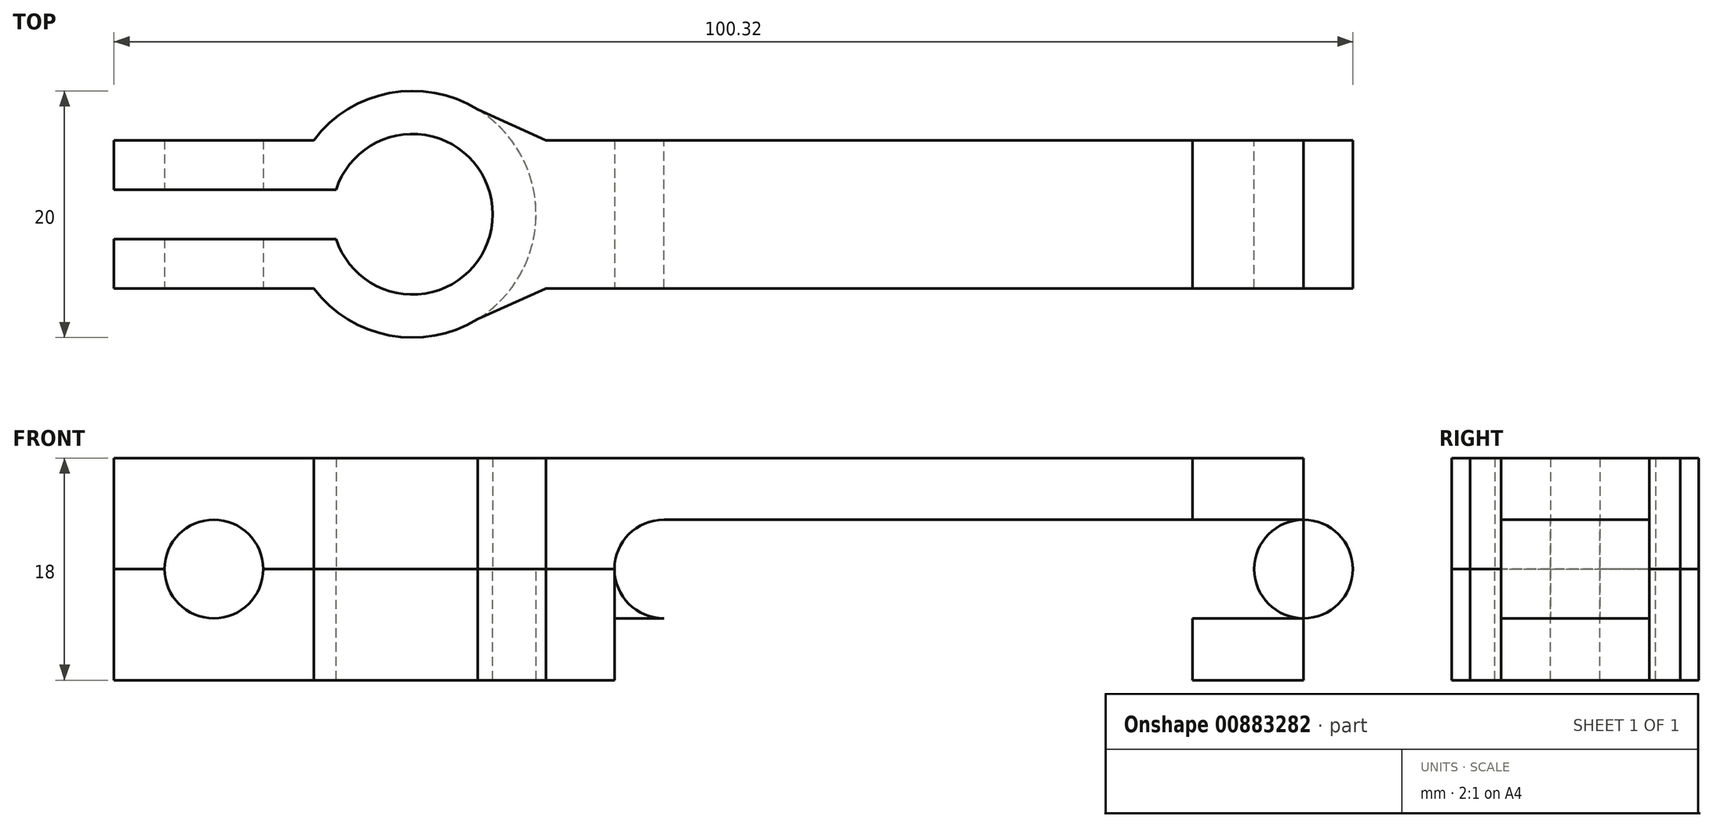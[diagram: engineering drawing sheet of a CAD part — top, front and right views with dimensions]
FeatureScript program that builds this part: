
annotation { "Feature Type Name" : "Feature", "Feature Type Description" : "" }
export const myFeature = defineFeature(function(context is Context, id is Id, definition is map)
    precondition{}
    {
        {
            var Q0;
            Q0=qCreatedBy(makeId("Top.planeOp"),FACE);
            var sketch = newSketch(context, id + "F0", { "sketchPlane" : qUnion([Q0])});
            skLineSegment(sketch, "E0", {"start": v(16.35, 0) * mm, "end": v(16.35, 6) * mm});
            skLineSegment(sketch, "E1", {"start": v(16.35, 6) * mm, "end": v(16.35, -6) * mm});
            skLineSegment(sketch, "E2", {"start": v(12.35, 0) * mm, "end": v(63.15, 0) * mm});
            skLineSegment(sketch, "E3", {"start": v(16.35, 6) * mm, "end": v(62.2, 6) * mm});
            skLineSegment(sketch, "E4", {"start": v(16.35, -6) * mm, "end": v(62.2, -6) * mm});
            skLineSegment(sketch, "E5", {"start": v(81.15, -2.5) * mm, "end": v(81.15, 2.5) * mm});
            skLineSegment(sketch, "E6", {"start": v(-8.1, 2) * mm, "end": v(-24.17, 2) * mm});
            skLineSegment(sketch, "E7", {"start": v(-8.1, -2) * mm, "end": v(-24.17, -2) * mm});
            skLineSegment(sketch, "E8", {"start": v(64.1, 2.5) * mm, "end": v(81.15, 2.5) * mm});
            skLineSegment(sketch, "E9.MirrorCS", {"start": v(64.1, -2.5) * mm, "end": v(81.15, -2.5) * mm});
            skLineSegment(sketch, "E10", {"start": v(63.15, 5.05) * mm, "end": v(63.15, 3.45) * mm});
            skLineSegment(sketch, "E11", {"start": v(63.15, -3.45) * mm, "end": v(63.15, -5.05) * mm});
            skPoint(sketch, "E12.visualSharp", {"position": v(63.15, 2.5) * mm});
            skPoint(sketch, "E13.visualSharp", {"position": v(63.15, -2.5) * mm});
            skPoint(sketch, "E14.visualSharp", {"position": v(63.15, -6) * mm});
            skPoint(sketch, "E15.visualSharp", {"position": v(63.15, 6) * mm});
            skLineSegment(sketch, "E16", {"start": v(63.15, 3.45) * mm, "end": v(63.15, -3.45) * mm});
            skLineSegment(sketch, "E17", {"start": v(63.15, 2.5) * mm, "end": v(64.1, 2.5) * mm});
            skLineSegment(sketch, "E18", {"start": v(64.1, -2.5) * mm, "end": v(63.15, -2.5) * mm});
            skLineSegment(sketch, "E19", {"start": v(62.2, -6) * mm, "end": v(63.15, -6) * mm});
            skLineSegment(sketch, "E20", {"start": v(63.15, -5.05) * mm, "end": v(63.15, -6) * mm});
            skLineSegment(sketch, "E21", {"start": v(62.2, 6) * mm, "end": v(63.15, 6) * mm});
            skLineSegment(sketch, "E22", {"start": v(63.15, 5.05) * mm, "end": v(63.15, 6) * mm});
            skArc(sketch, "E23", {"start": v(-6.18, -2) * mm, "mid": v(6.5, 0) * mm, "end": v(-6.18, 2) * mm});
            skLineSegment(sketch, "E24", {"start": v(-8.1, 2) * mm, "end": v(-6.18, 2) * mm});
            skLineSegment(sketch, "E25", {"start": v(-8.1, -2) * mm, "end": v(-6.18, -2) * mm});
            skLineSegment(sketch, "E26", {"start": v(-10.17, -7) * mm, "end": v(-24.17, -7) * mm});
            skLineSegment(sketch, "E27.trimOffspring", {"start": v(-24.17, 2) * mm, "end": v(-24.17, 6) * mm});
            skArc(sketch, "E28", {"start": v(-8, -6) * mm, "mid": v(10, 0) * mm, "end": v(-8, 6) * mm});
            skLineSegment(sketch, "E29", {"start": v(16.35, -6) * mm, "end": v(10.8, -6) * mm});
            skLineSegment(sketch, "E30", {"start": v(10.8, -6) * mm, "end": v(5.28, -8.5) * mm});
            skLineSegment(sketch, "E31.MirrorCS", {"start": v(16.35, 6) * mm, "end": v(10.8, 6) * mm});
            skLineSegment(sketch, "E32.MirrorCS", {"start": v(10.8, 6) * mm, "end": v(5.28, 8.5) * mm});
            skLineSegment(sketch, "E33", {"start": v(-24.17, 6) * mm, "end": v(-8, 6) * mm});
            skLineSegment(sketch, "E34.MirrorCS", {"start": v(-24.17, -6) * mm, "end": v(-8, -6) * mm});
            skLineSegment(sketch, "E35.MirrorCS", {"start": v(-24.17, -2) * mm, "end": v(-24.17, -6) * mm});
            skSolve(sketch);
        }
        {
            var Q0;
            Q0=makeQuery(id+"F0.imprint","IMPRINT",FACE,{"disambiguationData":[TD([[makeQuery(id+"F0.imprint","IMPRINT",EDGE,{"derivedFrom":sQuery(id+"F0.wireOp",EDGE,"E6")}),-1.0]])]});
            extrude(context, id + "F1", {"entities" : qUnion([Q0]), "depth" : 9 * mm, "offsetDistance" : 25 * mm});
        }
        {
            var Q0;
            {var subQ4=sQuery(id+"F0.wireOp",EDGE,"E1");Q0=makeQuery(id+"F0.imprint","IMPRINT",FACE,{"disambiguationData":[TD([[makeQuery(id+"F0.imprint","IMPRINT",EDGE,{"derivedFrom":subQ4}),1.0]])]});}
            var Q1;
            {var subQ4=sQuery(id+"F0.wireOp",EDGE,"E0");Q1=makeQuery(id+"F0.imprint","IMPRINT",FACE,{"disambiguationData":[TD([[makeQuery(id+"F0.imprint","IMPRINT",EDGE,{"derivedFrom":subQ4}),-1.0]])]});}
            var Q2;
            {var subQ0=sQuery(id+"F0.wireOp",EDGE,"26rSQapK-BJur-WUPp-nK8w-Sfx6okr37QMO");Q2=makeQuery(id+"F0.imprint","IMPRINT",FACE,{"disambiguationData":[TD([[makeQuery(id+"F0.imprint","IMPRINT",EDGE,{"derivedFrom":subQ0}),-1.0]])]});}
            var Q3;
            {var subQ0=sQuery(id+"F0.wireOp",EDGE,"FH9L3wZH-bFjv-XjhE-hYi4-qwH4n2wXpiqg");Q3=makeQuery(id+"F0.imprint","IMPRINT",FACE,{"disambiguationData":[TD([[makeQuery(id+"F0.imprint","IMPRINT",EDGE,{"derivedFrom":subQ0}),1.0]])]});}
            extrude(context, id + "F2", {"entities" : qUnion([Q0, Q1, Q2, Q3]), "depth" : 9 * mm, "offsetDistance" : 25 * mm});
        }
        {
            var Q0;
            Q0=makeQuery(id+"F2.opExtrude","SWEPT_FACE",FACE,{"disambiguationData":[OSD([sQuery(id+"F0.wireOp",EDGE,"E3"),sQuery(id+"F0.wireOp",EDGE,"E21")])]});
            var sketch = newSketch(context, id + "F3", { "sketchPlane" : qUnion([Q0])});
            skLineSegment(sketch, "E36", {"start": v(-63.15, 0) * mm, "end": v(-72.15, 0) * mm});
            skCircle(sketch, "E37", {"center": v(-72.15, 0) * mm, "radius": 9 * mm});
            skLineSegment(sketch, "E38", {"start": v(-72.15, 0) * mm, "end": v(-72.15, 9) * mm});
            skLineSegment(sketch, "E39", {"start": v(-16.35, 0) * mm, "end": v(-16.35, 9) * mm});
            skLineSegment(sketch, "E40", {"start": v(-16.35, 9) * mm, "end": v(-72.15, 9) * mm});
            skLineSegment(sketch, "E41", {"start": v(-16.35, 0) * mm, "end": v(-16.35, -4) * mm});
            skLineSegment(sketch, "E42", {"start": v(-16.35, -4) * mm, "end": v(-64.09, -4) * mm});
            skLineSegment(sketch, "E43", {"start": v(-47.67, 9) * mm, "end": v(-16.35, 9) * mm});
            skLineSegment(sketch, "E44", {"start": v(-47.67, 9) * mm, "end": v(-72.15, 9) * mm});
            skLineSegment(sketch, "E45", {"start": v(-64.09, -4) * mm, "end": v(-42.4, -4) * mm});
            skLineSegment(sketch, "E46", {"start": v(-63.15, 0) * mm, "end": v(-63.15, -4) * mm});
            skLineSegment(sketch, "E47", {"start": v(-63.15, -4) * mm, "end": v(-64.09, -4) * mm});
            skCircle(sketch, "E48", {"center": v(-72.15, 0) * mm, "radius": 4 * mm});
            skLineSegment(sketch, "E49", {"start": v(-72.15, 0) * mm, "end": v(-72.15, -9) * mm});
            skLineSegment(sketch, "E50", {"start": v(-72.15, -9) * mm, "end": v(-63.15, -9) * mm});
            skLineSegment(sketch, "E51", {"start": v(-63.15, -9) * mm, "end": v(-63.15, 0) * mm});
            skLineSegment(sketch, "E52", {"start": v(-72.15, 0) * mm, "end": v(-72.15, 4) * mm});
            skLineSegment(sketch, "E53", {"start": v(-16.35, 0) * mm, "end": v(-20.35, 0) * mm});
            skArc(sketch, "E54", {"start": v(-20.35, -4) * mm, "mid": v(-16.35, 0) * mm, "end": v(-20.35, 4) * mm});
            skLineSegment(sketch, "E55", {"start": v(-20.35, 0) * mm, "end": v(-20.35, 4) * mm});
            skLineSegment(sketch, "E56", {"start": v(-20.35, 4) * mm, "end": v(-72.15, 4) * mm});
            skLineSegment(sketch, "E57", {"start": v(-20.35, 0) * mm, "end": v(-20.35, -4) * mm});
            skLineSegment(sketch, "E58", {"start": v(-72.15, 0) * mm, "end": v(-72.15, -4) * mm});
            skLineSegment(sketch, "E59", {"start": v(-72.15, -4) * mm, "end": v(-20.35, -4) * mm});
            skLineSegment(sketch, "E60", {"start": v(-63.15, -4) * mm, "end": v(-63.15, -9) * mm});
            skLineSegment(sketch, "E61", {"start": v(-16.35, -4) * mm, "end": v(-63.15, -4) * mm});
            skLineSegment(sketch, "E62", {"start": v(-16.35, -4) * mm, "end": v(-16.35, -9) * mm});
            skLineSegment(sketch, "E63", {"start": v(-16.35, -9) * mm, "end": v(-63.15, -9) * mm});
            skSolve(sketch);
        }
        {
            var Q0;
            Q0=makeQuery(id+"F0.imprint","IMPRINT",FACE,{"disambiguationData":[TD([[makeQuery(id+"F0.imprint","IMPRINT",EDGE,{"derivedFrom":sQuery(id+"F0.wireOp",EDGE,"E0")}),1.0]])]});
            extrude(context, id + "F4", {"entities" : qUnion([Q0]), "operationType" : NewBodyOperationType.ADD, "depth" : 9 * mm, "offsetDistance" : 25 * mm});
        }
        {
            var Q0;
            Q0=makeQuery(id+"F0.imprint","IMPRINT",FACE,{"disambiguationData":[TD([[makeQuery(id+"F0.imprint","IMPRINT",EDGE,{"derivedFrom":sQuery(id+"F0.wireOp",EDGE,"E0")}),1.0]])]});
            extrude(context, id + "F5", {"entities" : qUnion([Q0]), "oppositeDirection" : true, "depth" : 9 * mm, "offsetDistance" : 25 * mm});
        }
        {
            var Q0;
            Q0=makeQuery(id+"F0.imprint","IMPRINT",FACE,{"disambiguationData":[TD([[makeQuery(id+"F0.imprint","IMPRINT",EDGE,{"derivedFrom":sQuery(id+"F0.wireOp",EDGE,"E6")}),-1.0]])]});
            extrude(context, id + "F6", {"entities" : qUnion([Q0]), "oppositeDirection" : true, "depth" : 9 * mm, "offsetDistance" : 25 * mm});
        }
        {
            var Q0;
            Q0=makeQuery(id+"F6.opExtrude","SWEPT_FACE",FACE,{"disambiguationData":[OSD([sQuery(id+"F0.wireOp",EDGE,"E34.MirrorCS")])]});
            var sketch = newSketch(context, id + "F7", { "sketchPlane" : qUnion([Q0])});
            skLineSegment(sketch, "E64", {"start": v(-24.17, 0) * mm, "end": v(-8, 0) * mm});
            skLineSegment(sketch, "E65", {"start": v(-8, 0) * mm, "end": v(-16.09, 0) * mm});
            skSolve(sketch);
        }
        {
            var Q0;
            Q0=sQuery(id+"F7.wireOp",VERTEX,"E65.end");
            var Q1;
            Q1=makeQuery(id+"F1.opExtrude","SWEPT_BODY",BODY,{"disambiguationData":[OSD([sQuery(id+"F0.wireOp",EDGE,"E6"),sQuery(id+"F0.wireOp",EDGE,"E7"),sQuery(id+"F0.wireOp",EDGE,"E23"),sQuery(id+"F0.wireOp",EDGE,"E24"),sQuery(id+"F0.wireOp",EDGE,"E25"),sQuery(id+"F0.wireOp",EDGE,"E27.trimOffspring"),sQuery(id+"F0.wireOp",EDGE,"E28"),sQuery(id+"F0.wireOp",EDGE,"E33"),sQuery(id+"F0.wireOp",EDGE,"E34.MirrorCS"),sQuery(id+"F0.wireOp",EDGE,"E35.MirrorCS")])]});
            var Q2;
            Q2=makeQuery(id+"F6.opExtrude","SWEPT_BODY",BODY,{"disambiguationData":[OSD([sQuery(id+"F0.wireOp",EDGE,"E6"),sQuery(id+"F0.wireOp",EDGE,"E7"),sQuery(id+"F0.wireOp",EDGE,"E23"),sQuery(id+"F0.wireOp",EDGE,"E24"),sQuery(id+"F0.wireOp",EDGE,"E25"),sQuery(id+"F0.wireOp",EDGE,"E27.trimOffspring"),sQuery(id+"F0.wireOp",EDGE,"E28"),sQuery(id+"F0.wireOp",EDGE,"E33"),sQuery(id+"F0.wireOp",EDGE,"E34.MirrorCS"),sQuery(id+"F0.wireOp",EDGE,"E35.MirrorCS")])]});
            hole(context, id + "F8", {"style" : HoleStyle.SIMPLE, "endStyle" : HoleEndStyle.THROUGH, "holeDiameter" : 8 * mm, "majorDiameter" : 5 * mm, "isTappedThrough" : true, "tappedDepth" : 12 * mm, "tapClearance" : 3, "locations" : qUnion([Q0]), "scope" : qUnion([Q1, Q2])});
        }
        {
            var Q0;
            {var subQ0=sQuery(id+"F3.wireOp",EDGE,"E55");Q0=makeQuery(id+"F3.imprint","IMPRINT",FACE,{"disambiguationData":[TD([[makeQuery(id+"F3.imprint","IMPRINT",EDGE,{"derivedFrom":subQ0}),1.0]])]});}
            var Q1;
            {var subQ0=sQuery(id+"F3.wireOp",EDGE,"E46");Q1=makeQuery(id+"F3.imprint","IMPRINT",FACE,{"disambiguationData":[TD([[makeQuery(id+"F3.imprint","IMPRINT",EDGE,{"derivedFrom":subQ0}),1.0]])]});}
            var Q2;
            {var subQ0=sQuery(id+"F3.wireOp",EDGE,"E53");Q2=makeQuery(id+"F3.imprint","IMPRINT",FACE,{"disambiguationData":[TD([[makeQuery(id+"F3.imprint","IMPRINT",EDGE,{"derivedFrom":subQ0}),1.0]])]});}
            var Q3;
            {var subQ0=sQuery(id+"F3.wireOp",EDGE,"E53");Q3=makeQuery(id+"F3.imprint","IMPRINT",FACE,{"disambiguationData":[TD([[makeQuery(id+"F3.imprint","IMPRINT",EDGE,{"derivedFrom":subQ0}),-1.0]])]});}
            var Q4;
            {var subQ1=sQuery(id+"F3.wireOp",EDGE,"E36");var subQ4=sQuery(id+"F3.wireOp",EDGE,"E48");var subQ5=makeQuery(id+"F3.imprint","INTERSECT",VERTEX,{"derivedFrom":[subQ1,subQ4]});Q4=makeQuery(id+"F3.imprint","IMPRINT",FACE,{"disambiguationData":[TD([[makeQuery(id+"F3.imprint","IMPRINT",EDGE,{"disambiguationData":[TD([[subQ5,-1.0]])],"derivedFrom":subQ4}),-1.0]])]});}
            var Q5;
            {var subQ1=sQuery(id+"F3.wireOp",EDGE,"E36");var subQ4=sQuery(id+"F3.wireOp",EDGE,"E48");var subQ5=makeQuery(id+"F3.imprint","INTERSECT",VERTEX,{"derivedFrom":[subQ1,subQ4]});Q5=makeQuery(id+"F3.imprint","IMPRINT",FACE,{"disambiguationData":[TD([[makeQuery(id+"F3.imprint","IMPRINT",EDGE,{"disambiguationData":[TD([[subQ5,1.0]])],"derivedFrom":subQ4}),-1.0]])]});}
            var Q6;
            {var subQ0=sQuery(id+"F3.wireOp",EDGE,"E37");var subQ4=sQuery(id+"F3.wireOp",EDGE,"E56");var subQ5=makeQuery(id+"F3.imprint","INTERSECT",VERTEX,{"derivedFrom":[subQ0,subQ4]});Q6=makeQuery(id+"F3.imprint","IMPRINT",FACE,{"disambiguationData":[TD([[makeQuery(id+"F3.imprint","IMPRINT",EDGE,{"disambiguationData":[TD([[subQ5,1.0]])],"derivedFrom":subQ4}),1.0]])]});}
            var Q7;
            {var subQ0=sQuery(id+"F3.wireOp",EDGE,"E46");Q7=makeQuery(id+"F3.imprint","IMPRINT",FACE,{"disambiguationData":[TD([[makeQuery(id+"F3.imprint","IMPRINT",EDGE,{"derivedFrom":subQ0}),-1.0]])]});}
            var Q8;
            {var subQ0=sQuery(id+"F3.wireOp",EDGE,"E52");Q8=makeQuery(id+"F3.imprint","IMPRINT",FACE,{"disambiguationData":[TD([[makeQuery(id+"F3.imprint","IMPRINT",EDGE,{"derivedFrom":subQ0}),-1.0]])]});}
            var Q9;
            {var subQ0=sQuery(id+"F3.wireOp",EDGE,"E58");Q9=makeQuery(id+"F3.imprint","IMPRINT",FACE,{"disambiguationData":[TD([[makeQuery(id+"F3.imprint","IMPRINT",EDGE,{"derivedFrom":subQ0}),1.0]])]});}
            var Q10;
            {var subQ0=sQuery(id+"F3.wireOp",EDGE,"E52");Q10=makeQuery(id+"F3.imprint","IMPRINT",FACE,{"disambiguationData":[TD([[makeQuery(id+"F3.imprint","IMPRINT",EDGE,{"derivedFrom":subQ0}),1.0]])]});}
            extrude(context, id + "F9", {"entities" : qUnion([Q0, Q1, Q2, Q3, Q4, Q5, Q6, Q7, Q8, Q9, Q10]), "operationType" : NewBodyOperationType.REMOVE, "oppositeDirection" : true, "depth" : 25 * mm, "offsetDistance" : 25 * mm});
        }
        {
            var Q0;
            {var subQ1=sQuery(id+"F3.wireOp",EDGE,"E37");var subQ3=sQuery(id+"F3.wireOp",EDGE,"E56");var subQ4=makeQuery(id+"F3.imprint","INTERSECT",VERTEX,{"derivedFrom":[subQ1,subQ3]});Q0=makeQuery(id+"F3.imprint","IMPRINT",FACE,{"disambiguationData":[TD([[makeQuery(id+"F3.imprint","IMPRINT",EDGE,{"disambiguationData":[TD([[subQ4,-1.0]])],"derivedFrom":subQ1}),-1.0]])]});}
            var Q1;
            {var subQ0=sQuery(id+"F3.wireOp",EDGE,"E38");Q1=makeQuery(id+"F3.imprint","IMPRINT",FACE,{"disambiguationData":[TD([[makeQuery(id+"F3.imprint","IMPRINT",EDGE,{"derivedFrom":subQ0}),-1.0]])]});}
            var Q2;
            {var subQ0=sQuery(id+"F3.wireOp",EDGE,"E50");Q2=makeQuery(id+"F3.imprint","IMPRINT",FACE,{"disambiguationData":[TD([[makeQuery(id+"F3.imprint","IMPRINT",EDGE,{"derivedFrom":subQ0}),1.0]])]});}
            var Q3;
            {var subQ0=sQuery(id+"F3.wireOp",EDGE,"E49");Q3=makeQuery(id+"F3.imprint","IMPRINT",FACE,{"disambiguationData":[TD([[makeQuery(id+"F3.imprint","IMPRINT",EDGE,{"derivedFrom":subQ0}),1.0]])]});}
            extrude(context, id + "F10", {"entities" : qUnion([Q0, Q1, Q2, Q3]), "oppositeDirection" : true, "depth" : 12 * mm, "offsetDistance" : 25 * mm});
        }
        {
            var Q0;
            {var subQ1=sQuery(id+"F3.wireOp",EDGE,"E60");Q0=makeQuery(id+"F3.imprint","IMPRINT",FACE,{"disambiguationData":[TD([[makeQuery(id+"F3.imprint","IMPRINT",EDGE,{"derivedFrom":subQ1}),1.0]])]});}
            var Q1;
            {var subQ0=sQuery(id+"F3.wireOp",EDGE,"E41");Q1=makeQuery(id+"F3.imprint","IMPRINT",FACE,{"disambiguationData":[TD([[makeQuery(id+"F3.imprint","IMPRINT",EDGE,{"derivedFrom":subQ0}),-1.0]])]});}
            extrude(context, id + "F11", {"entities" : qUnion([Q0, Q1]), "oppositeDirection" : true, "depth" : 12 * mm, "offsetDistance" : 25 * mm});
        }
        {
            var Q0;
            {var subQ0=sQuery(id+"F3.wireOp",EDGE,"E38");Q0=makeQuery(id+"F3.imprint","IMPRINT",FACE,{"disambiguationData":[TD([[makeQuery(id+"F3.imprint","IMPRINT",EDGE,{"derivedFrom":subQ0}),1.0]])]});}
            extrude(context, id + "F12", {"entities" : qUnion([Q0]), "oppositeDirection" : true, "depth" : 12 * mm, "offsetDistance" : 25 * mm});
        }
    });
